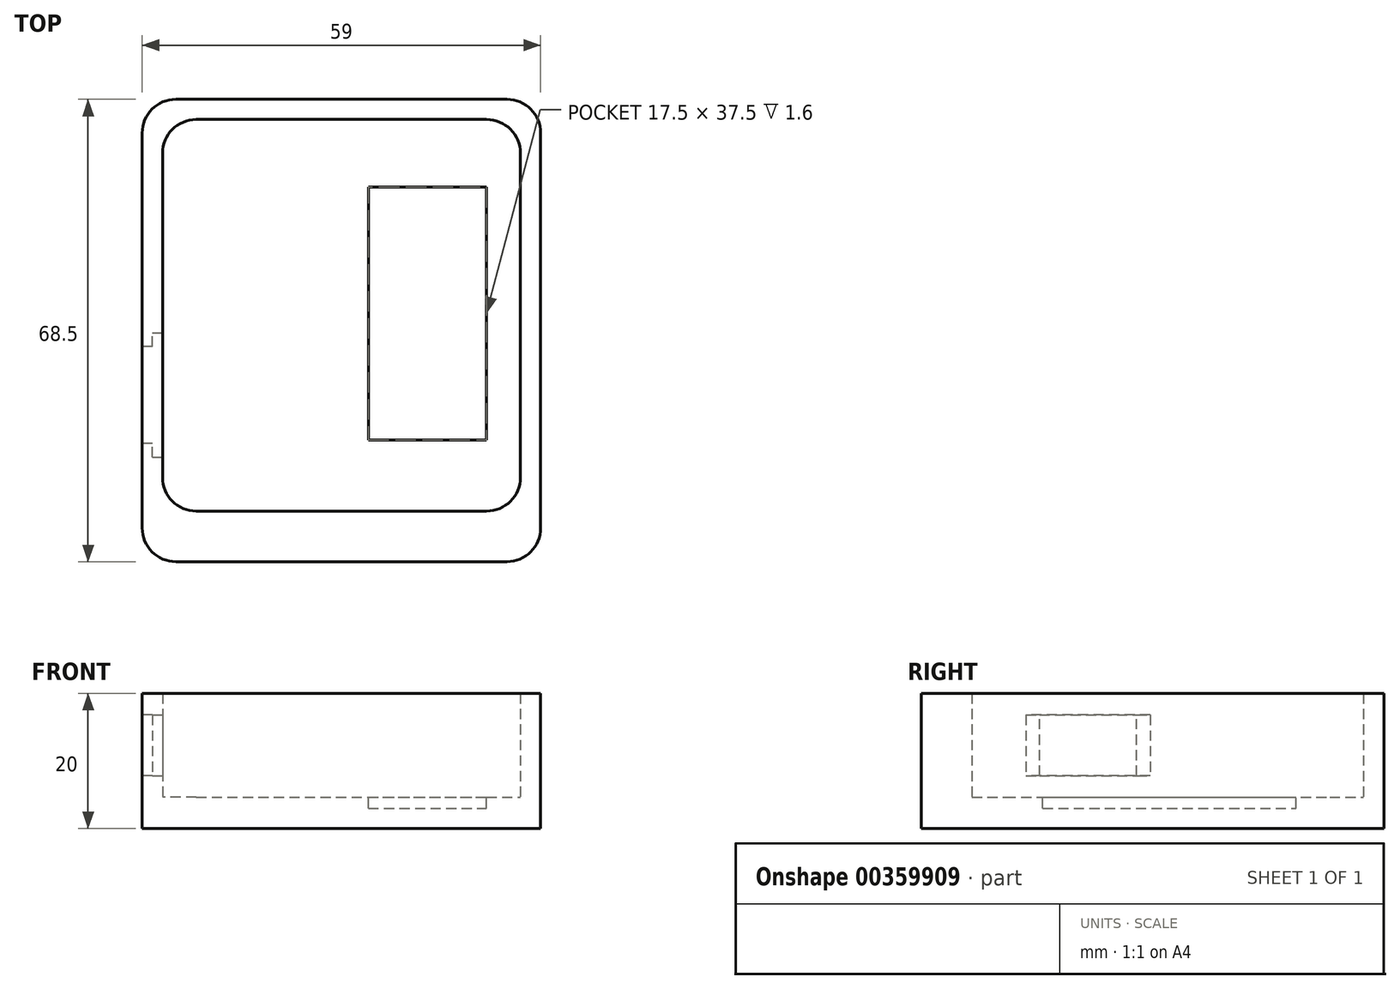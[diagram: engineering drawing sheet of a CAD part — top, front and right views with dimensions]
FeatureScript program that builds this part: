
annotation { "Feature Type Name" : "Feature", "Feature Type Description" : "" }
export const myFeature = defineFeature(function(context is Context, id is Id, definition is map)
    precondition{}
    {
        {
            var Q0;
            Q0=qCreatedBy(makeId("Top.planeOp"),FACE);
            var sketch = newSketch(context, id + "F0", { "sketchPlane" : qUnion([Q0])});
            skLineSegment(sketch, "E0.bottom", {"start": v(-18.75, 8.75) * mm, "end": v(18.75, 8.75) * mm});
            skLineSegment(sketch, "E0.top", {"start": v(-18.75, -8.75) * mm, "end": v(18.75, -8.75) * mm});
            skLineSegment(sketch, "E0.left", {"start": v(-18.75, 8.75) * mm, "end": v(-18.75, -8.75) * mm});
            skLineSegment(sketch, "E0.right", {"start": v(18.75, 8.75) * mm, "end": v(18.75, -8.75) * mm});
            skPoint(sketch, "E0.middle", {"position": v(0, 0) * mm});
            skLineSegment(sketch, "E1.bottom", {"start": v(-23.75, 13.75) * mm, "end": v(23.75, 13.75) * mm});
            skLineSegment(sketch, "E1.top", {"start": v(-23.75, -13.75) * mm, "end": v(23.75, -13.75) * mm});
            skLineSegment(sketch, "E1.left", {"start": v(-23.75, 13.75) * mm, "end": v(-23.75, -13.75) * mm});
            skLineSegment(sketch, "E1.right", {"start": v(23.75, 13.75) * mm, "end": v(23.75, -13.75) * mm});
            skSolve(sketch);
        }
        {
            var Q0;
            Q0=makeQuery(id+"F0.imprint","IMPRINT",FACE,{"disambiguationData":[TD([[makeQuery(id+"F0.imprint","IMPRINT",EDGE,{"derivedFrom":sQuery(id+"F0.wireOp",EDGE,"E0.bottom")}),-1.0]])]});
            var Q1;
            Q1=makeQuery(id+"F0.imprint","IMPRINT",FACE,{"disambiguationData":[TD([[makeQuery(id+"F0.imprint","IMPRINT",EDGE,{"derivedFrom":sQuery(id+"F0.wireOp",EDGE,"E0.bottom")}),1.0]])]});
            extrude(context, id + "F1", {"entities" : qUnion([Q0, Q1]), "depth" : 4.6 * mm});
        }
        {
            var Q0;
            Q0=makeQuery(id+"F0.imprint","IMPRINT",FACE,{"disambiguationData":[TD([[makeQuery(id+"F0.imprint","IMPRINT",EDGE,{"derivedFrom":sQuery(id+"F0.wireOp",EDGE,"E0.bottom")}),-1.0]])]});
            extrude(context, id + "F2", {"entities" : qUnion([Q0]), "operationType" : NewBodyOperationType.REMOVE, "depth" : 1.6 * mm});
        }
        {
            var Q0;
            Q0=qCreatedBy(makeId("Top.planeOp"),FACE);
            cPlane(context, id + "F3", {"entities" : qUnion([Q0]), "cplaneType" : CPlaneType.OFFSET, "offset" : (4.6 / 2) * mm, "width" : 150 * mm, "height" : 150 * mm});
        }
        {
            var Q0;
            Q0=makeQuery(id+"F1.opExtrude","SWEPT_BODY",BODY,{"disambiguationData":[OSD([sQuery(id+"F0.wireOp",EDGE,"E1.bottom"),sQuery(id+"F0.wireOp",EDGE,"E1.top"),sQuery(id+"F0.wireOp",EDGE,"E1.left"),sQuery(id+"F0.wireOp",EDGE,"E1.right")])]});
            var Q1;
            Q1=qCreatedBy(id+"F3.planeOp",FACE);
            mirror(context, id + "F4", {"entities" : qUnion([Q0]), "mirrorPlane" : qUnion([Q1])});
        }
        {
            var Q0;
            Q0=makeQuery(id+"F1.opExtrude","SWEPT_BODY",BODY,{"disambiguationData":[OSD([sQuery(id+"F0.wireOp",EDGE,"E1.bottom"),sQuery(id+"F0.wireOp",EDGE,"E1.top"),sQuery(id+"F0.wireOp",EDGE,"E1.left"),sQuery(id+"F0.wireOp",EDGE,"E1.right")])]});
            deleteBodies(context, id + "F5", {"entities" : qUnion([Q0])});
        }
        {
            var Q0;
            Q0=qCreatedBy(makeId("Right.planeOp"),FACE);
            var sketch = newSketch(context, id + "F6", { "sketchPlane" : qUnion([Q0])});
            skLineSegment(sketch, "E2", {"start": v(0, 0) * mm, "end": v(0, 32.45) * mm});
            skSolve(sketch);
        }
        {
            var Q0;
            Q0=makeQuery(id+"F4.opPattern","COPY",BODY,{"derivedFrom":makeQuery(id+"F1.opExtrude","SWEPT_BODY",BODY,{"disambiguationData":[OSD([sQuery(id+"F0.wireOp",EDGE,"E1.bottom"),sQuery(id+"F0.wireOp",EDGE,"E1.top"),sQuery(id+"F0.wireOp",EDGE,"E1.left"),sQuery(id+"F0.wireOp",EDGE,"E1.right")])]}),"instanceName":"1"});
            var Q1;
            Q1=sQuery(id+"F6.wireOp",EDGE,"E2");
            transform(context, id + "F7", {"entities" : qUnion([Q0]), "transformType" : TransformType.ROTATION, "transformAxis" : qUnion([Q1]), "angle" : 90 * degree, "makeCopy" : false});
        }
        {
            var Q0;
            Q0=qCreatedBy(makeId("Top.planeOp"),FACE);
            var sketch = newSketch(context, id + "F8", { "sketchPlane" : qUnion([Q0])});
            skArc(sketch, "E3", {"start": v(-37.25, 31.75) * mm, "mid": v(-40.79, 30.29) * mm, "end": v(-42.25, 26.75) * mm});
            skArc(sketch, "E4", {"start": v(16.75, 26.75) * mm, "mid": v(15.29, 30.29) * mm, "end": v(11.75, 31.75) * mm});
            skArc(sketch, "E5", {"start": v(11.75, -36.75) * mm, "mid": v(15.29, -35.29) * mm, "end": v(16.75, -31.75) * mm});
            skArc(sketch, "E6", {"start": v(-42.25, -31.75) * mm, "mid": v(-40.79, -35.29) * mm, "end": v(-37.25, -36.75) * mm});
            skLineSegment(sketch, "E7", {"start": v(-37.25, -36.75) * mm, "end": v(11.75, -36.75) * mm});
            skLineSegment(sketch, "E8", {"start": v(16.75, -31.75) * mm, "end": v(16.75, 26.75) * mm});
            skLineSegment(sketch, "E9", {"start": v(11.75, 31.75) * mm, "end": v(-37.25, 31.75) * mm});
            skLineSegment(sketch, "E10", {"start": v(-42.25, 26.75) * mm, "end": v(-42.25, -31.75) * mm});
            skLineSegment(sketch, "E11", {"start": v(-39.25, -24.25) * mm, "end": v(-39.25, 23.75) * mm});
            skArc(sketch, "E12", {"start": v(-34.25, 28.75) * mm, "mid": v(-37.79, 27.29) * mm, "end": v(-39.25, 23.75) * mm});
            skArc(sketch, "E13", {"start": v(13.75, 23.75) * mm, "mid": v(12.29, 27.29) * mm, "end": v(8.75, 28.75) * mm});
            skArc(sketch, "E14", {"start": v(8.75, -29.25) * mm, "mid": v(12.29, -27.79) * mm, "end": v(13.75, -24.25) * mm});
            skArc(sketch, "E15", {"start": v(-39.25, -24.25) * mm, "mid": v(-37.79, -27.79) * mm, "end": v(-34.25, -29.25) * mm});
            skLineSegment(sketch, "E16", {"start": v(-34.25, -29.25) * mm, "end": v(8.75, -29.25) * mm});
            skLineSegment(sketch, "E17", {"start": v(13.75, -24.25) * mm, "end": v(13.75, 23.75) * mm});
            skLineSegment(sketch, "E18", {"start": v(8.75, 28.75) * mm, "end": v(-34.25, 28.75) * mm});
            skLineSegment(sketch, "E19.bottom", {"start": v(-8.75, 18.75) * mm, "end": v(8.75, 18.75) * mm});
            skLineSegment(sketch, "E19.top", {"start": v(-8.75, -18.75) * mm, "end": v(8.75, -18.75) * mm});
            skLineSegment(sketch, "E19.left", {"start": v(-8.75, 18.75) * mm, "end": v(-8.75, -18.75) * mm});
            skLineSegment(sketch, "E19.right", {"start": v(8.75, 18.75) * mm, "end": v(8.75, -18.75) * mm});
            skSolve(sketch);
        }
        {
            var Q0;
            Q0=makeQuery(id+"F8.imprint","IMPRINT",FACE,{"disambiguationData":[TD([[makeQuery(id+"F8.imprint","IMPRINT",EDGE,{"derivedFrom":sQuery(id+"F8.wireOp",EDGE,"E11")}),-1.0]])]});
            var Q1;
            Q1=makeQuery(id+"F8.imprint","IMPRINT",FACE,{"disambiguationData":[TD([[makeQuery(id+"F8.imprint","IMPRINT",EDGE,{"derivedFrom":sQuery(id+"F8.wireOp",EDGE,"E3")}),1.0]])]});
            var Q2;
            Q2=makeQuery(id+"F4.opPattern","COPY",FACE,{"derivedFrom":makeQuery(id+"F1.opExtrude","CAP_FACE",FACE,{"disambiguationData":[OSD([sQuery(id+"F0.wireOp",EDGE,"E1.bottom"),sQuery(id+"F0.wireOp",EDGE,"E1.top"),sQuery(id+"F0.wireOp",EDGE,"E1.left"),sQuery(id+"F0.wireOp",EDGE,"E1.right")])],"isStart":true}),"instanceName":"1"});
            extrude(context, id + "F9", {"entities" : qUnion([Q0, Q1]), "operationType" : NewBodyOperationType.ADD, "endBound" : BoundingType.UP_TO_SURFACE, "endBoundEntityFace" : qUnion([Q2]), "depth" : 25 * mm});
        }
        {
            var Q0;
            Q0=makeQuery(id+"F8.imprint","IMPRINT",FACE,{"disambiguationData":[TD([[makeQuery(id+"F8.imprint","IMPRINT",EDGE,{"derivedFrom":sQuery(id+"F8.wireOp",EDGE,"E3")}),1.0]])]});
            extrude(context, id + "F10", {"entities" : qUnion([Q0]), "operationType" : NewBodyOperationType.ADD, "depth" : 20 * mm});
        }
        {
            var Q0;
            {var subQ0=sQuery(id+"F8.wireOp",EDGE,"E10");Q0=makeQuery(id+"F10.boolean.opBoolean","MERGE",FACE,{"derivedFrom":[makeQuery(id+"F9.opExtrude","SWEPT_FACE",FACE,{"disambiguationData":[OSD([subQ0])]}),makeQuery(id+"F10.opExtrude","SWEPT_FACE",FACE,{"disambiguationData":[OSD([subQ0])]})]});}
            var sketch = newSketch(context, id + "F11", { "sketchPlane" : qUnion([Q0])});
            skLineSegment(sketch, "E20.bottom", {"start": v(19.25, 7.8) * mm, "end": v(4.85, 7.8) * mm});
            skLineSegment(sketch, "E20.top", {"start": v(19.25, 16.8) * mm, "end": v(4.85, 16.8) * mm});
            skLineSegment(sketch, "E20.left", {"start": v(19.25, 7.8) * mm, "end": v(19.25, 16.8) * mm});
            skLineSegment(sketch, "E20.right", {"start": v(4.85, 7.8) * mm, "end": v(4.85, 16.8) * mm});
            skPoint(sketch, "E21", {"position": v(19.25, 12.3) * mm});
            skLineSegment(sketch, "E22", {"start": v(19.25, 12.3) * mm, "end": v(19.25, 20) * mm, "construction": true});
            skLineSegment(sketch, "E23", {"start": v(19.25, 12.3) * mm, "end": v(19.25, 4.6) * mm, "construction": true});
            skSolve(sketch);
        }
        {
            var Q0;
            Q0=makeQuery(id+"F11.imprint","IMPRINT",FACE,{"disambiguationData":[TD([[makeQuery(id+"F11.imprint","IMPRINT",EDGE,{"derivedFrom":sQuery(id+"F11.wireOp",EDGE,"E20.bottom")}),-1.0]])]});
            extrude(context, id + "F12", {"entities" : qUnion([Q0]), "operationType" : NewBodyOperationType.REMOVE, "endBound" : BoundingType.UP_TO_NEXT, "oppositeDirection" : true, "depth" : 25 * mm});
        }
        {
            var Q0;
            Q0=makeQuery(id+"F10.opExtrude","SWEPT_FACE",FACE,{"disambiguationData":[OSD([sQuery(id+"F8.wireOp",EDGE,"E11")])]});
            var sketch = newSketch(context, id + "F13", { "sketchPlane" : qUnion([Q0])});
            skLineSegment(sketch, "E24.bottom", {"start": v(-21.25, 16.8) * mm, "end": v(-2.85, 16.8) * mm});
            skLineSegment(sketch, "E24.top", {"start": v(-21.25, 7.8) * mm, "end": v(-2.85, 7.8) * mm});
            skLineSegment(sketch, "E24.left", {"start": v(-21.25, 16.8) * mm, "end": v(-21.25, 7.8) * mm});
            skLineSegment(sketch, "E24.right", {"start": v(-2.85, 16.8) * mm, "end": v(-2.85, 7.8) * mm});
            skSolve(sketch);
        }
        {
            var Q0;
            {var subQ2=sQuery(id+"F13.wireOp",EDGE,"E24.left");Q0=makeQuery(id+"F13.imprint","IMPRINT",FACE,{"disambiguationData":[TD([[makeQuery(id+"F13.imprint","IMPRINT",EDGE,{"derivedFrom":subQ2}),1.0]])]});}
            var Q1;
            {var subQ2=sQuery(id+"F13.wireOp",EDGE,"E24.right");Q1=makeQuery(id+"F13.imprint","IMPRINT",FACE,{"disambiguationData":[TD([[makeQuery(id+"F13.imprint","IMPRINT",EDGE,{"derivedFrom":subQ2}),-1.0]])]});}
            extrude(context, id + "F14", {"entities" : qUnion([Q0, Q1]), "operationType" : NewBodyOperationType.REMOVE, "oppositeDirection" : true, "depth" : 1.5 * mm});
        }
    });
